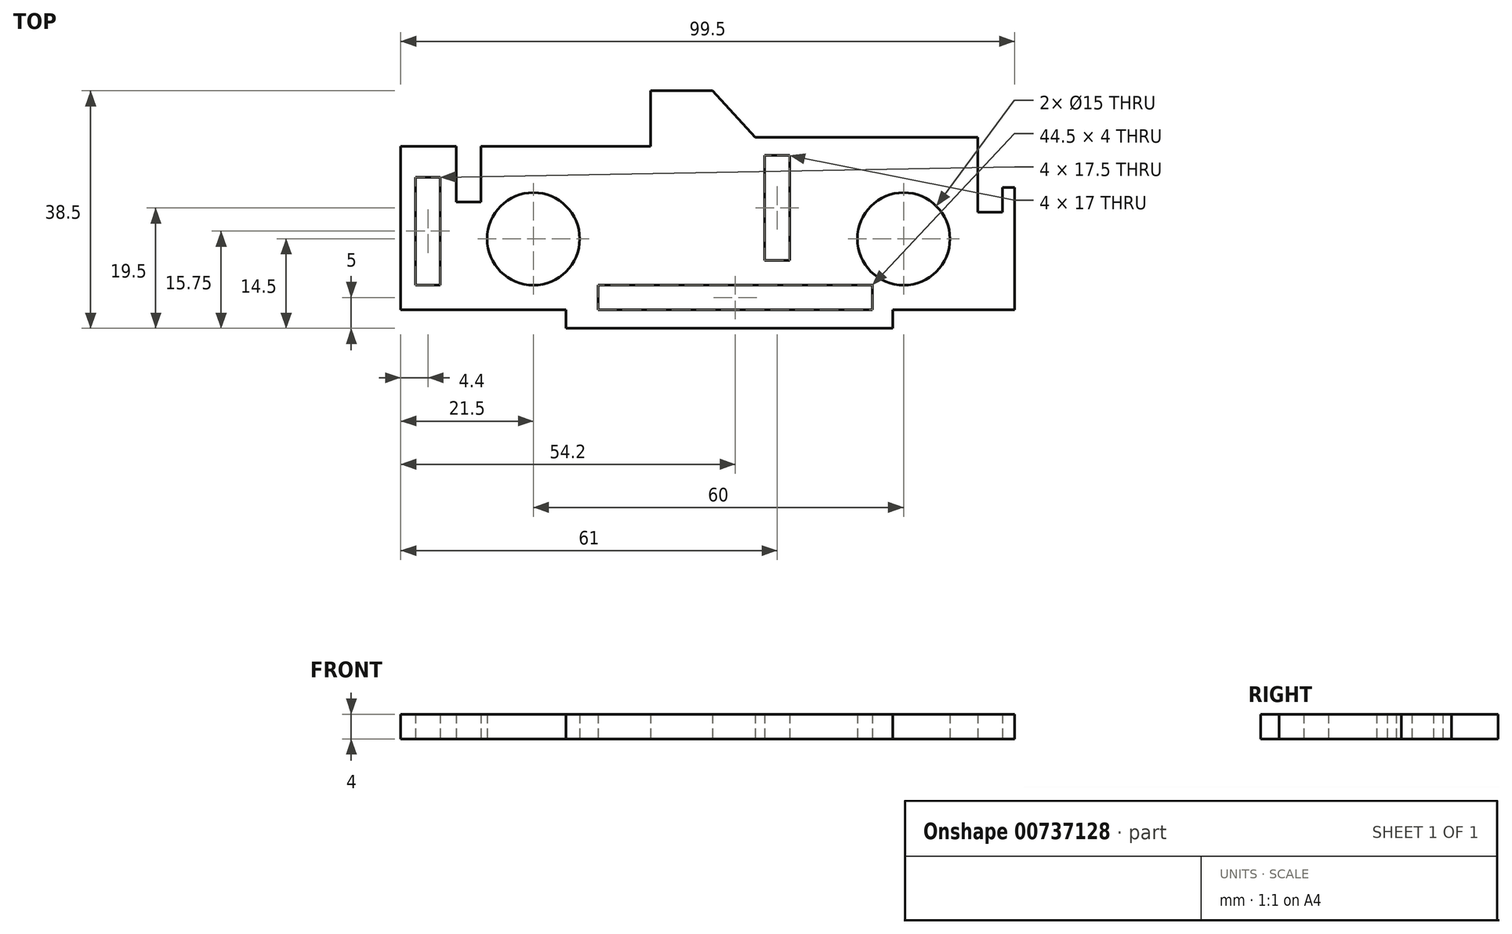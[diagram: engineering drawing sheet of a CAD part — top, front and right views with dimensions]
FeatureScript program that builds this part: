
annotation { "Feature Type Name" : "Feature", "Feature Type Description" : "" }
export const myFeature = defineFeature(function(context is Context, id is Id, definition is map)
    precondition{}
    {
        {
            var Q0;
            Q0=qCreatedBy(makeId("Top.planeOp"),FACE);
            var sketch = newSketch(context, id + "F0", { "sketchPlane" : qUnion([Q0])});
            skLineSegment(sketch, "E0.bottom", {"start": v(0, 0) * mm, "end": v(9, 0) * mm});
            skLineSegment(sketch, "E0.left", {"start": v(0, 0) * mm, "end": v(0, -26.5) * mm});
            skLineSegment(sketch, "E1", {"start": v(79.75, -26.5) * mm, "end": v(79.75, -29.5) * mm});
            skLineSegment(sketch, "E2", {"start": v(79.75, -29.5) * mm, "end": v(26.75, -29.5) * mm});
            skLineSegment(sketch, "E3", {"start": v(79.75, -26.5) * mm, "end": v(99.5, -26.5) * mm});
            skLineSegment(sketch, "E4", {"start": v(26.75, -29.5) * mm, "end": v(26.75, -26.5) * mm});
            skLineSegment(sketch, "E5", {"start": v(26.75, -26.5) * mm, "end": v(0, -26.5) * mm});
            skLineSegment(sketch, "E6", {"start": v(79.75, -26.5) * mm, "end": v(76.45, -26.5) * mm});
            skLineSegment(sketch, "E7", {"start": v(76.45, -26.5) * mm, "end": v(31.95, -26.5) * mm});
            skLineSegment(sketch, "E8", {"start": v(76.45, -26.5) * mm, "end": v(76.45, -22.5) * mm});
            skLineSegment(sketch, "E9", {"start": v(76.45, -22.5) * mm, "end": v(31.95, -22.5) * mm});
            skLineSegment(sketch, "E10", {"start": v(31.95, -22.5) * mm, "end": v(31.95, -26.5) * mm});
            skLineSegment(sketch, "E11", {"start": v(31.95, -26.5) * mm, "end": v(26.75, -26.5) * mm});
            skLineSegment(sketch, "E12.bottom", {"start": v(6.4, -22.5) * mm, "end": v(2.4, -22.5) * mm});
            skLineSegment(sketch, "E12.top", {"start": v(6.4, -5) * mm, "end": v(2.4, -5) * mm});
            skLineSegment(sketch, "E12.left", {"start": v(6.4, -22.5) * mm, "end": v(6.4, -5) * mm});
            skLineSegment(sketch, "E12.right", {"start": v(2.4, -22.5) * mm, "end": v(2.4, -5) * mm});
            skPoint(sketch, "E12.middle", {"position": v(4.4, -13.75) * mm});
            skLineSegment(sketch, "E13", {"start": v(9, 0) * mm, "end": v(9, -9) * mm});
            skLineSegment(sketch, "E14", {"start": v(9, -9) * mm, "end": v(13, -9) * mm});
            skLineSegment(sketch, "E15", {"start": v(13, 0) * mm, "end": v(13, -9) * mm});
            skCircle(sketch, "E16", {"center": v(21.5, -15) * mm, "radius": 7.5 * mm});
            skCircle(sketch, "E17", {"center": v(81.5, -15) * mm, "radius": 7.5 * mm});
            skLineSegment(sketch, "E18", {"start": v(21.5, -15) * mm, "end": v(81.5, -15) * mm, "construction": true});
            skLineSegment(sketch, "E19.bottom", {"start": v(59, -1.5) * mm, "end": v(63, -1.5) * mm});
            skLineSegment(sketch, "E19.top", {"start": v(59, -18.5) * mm, "end": v(63, -18.5) * mm});
            skLineSegment(sketch, "E19.left", {"start": v(59, -1.5) * mm, "end": v(59, -18.5) * mm});
            skLineSegment(sketch, "E19.right", {"start": v(63, -1.5) * mm, "end": v(63, -18.5) * mm});
            skPoint(sketch, "E20", {"position": v(93.5, 1.44) * mm});
            skPoint(sketch, "E21", {"position": v(99.5, -6.7) * mm});
            skLineSegment(sketch, "E22", {"start": v(93.5, 1.44) * mm, "end": v(93.5, -10.7) * mm});
            skLineSegment(sketch, "E23", {"start": v(93.5, -10.7) * mm, "end": v(97.5, -10.7) * mm});
            skLineSegment(sketch, "E24", {"start": v(97.5, -10.7) * mm, "end": v(97.5, -6.7) * mm});
            skLineSegment(sketch, "E25", {"start": v(97.5, -6.7) * mm, "end": v(99.5, -6.7) * mm});
            skLineSegment(sketch, "E26", {"start": v(99.5, -6.7) * mm, "end": v(99.5, -26.5) * mm});
            skLineSegment(sketch, "E27", {"start": v(40.5, 9) * mm, "end": v(50.5, 9) * mm});
            skLineSegment(sketch, "E28", {"start": v(50.5, 9) * mm, "end": v(57.45, 1.44) * mm});
            skLineSegment(sketch, "E29", {"start": v(57.45, 1.44) * mm, "end": v(93.5, 1.44) * mm});
            skLineSegment(sketch, "E30", {"start": v(13, 0) * mm, "end": v(40.5, 0) * mm});
            skLineSegment(sketch, "E31", {"start": v(40.5, 0) * mm, "end": v(40.5, 9) * mm});
            skSolve(sketch);
        }
        {
            var Q0;
            Q0=makeQuery(id+"F0.imprint","IMPRINT",FACE,{"disambiguationData":[TD([[makeQuery(id+"F0.imprint","IMPRINT",EDGE,{"derivedFrom":sQuery(id+"F0.wireOp",EDGE,"E0.bottom")}),-1.0]])]});
            var Q1;
            Q1=makeQuery(id+"F0.imprint","IMPRINT",FACE,{"disambiguationData":[TD([[makeQuery(id+"F0.imprint","IMPRINT",EDGE,{"derivedFrom":sQuery(id+"F0.wireOp",EDGE,"E1")}),-1.0]])]});
            extrude(context, id + "F1", {"entities" : qUnion([Q0, Q1]), "depth" : 4 * mm, "offsetDistance" : 25 * mm});
        }
    });
